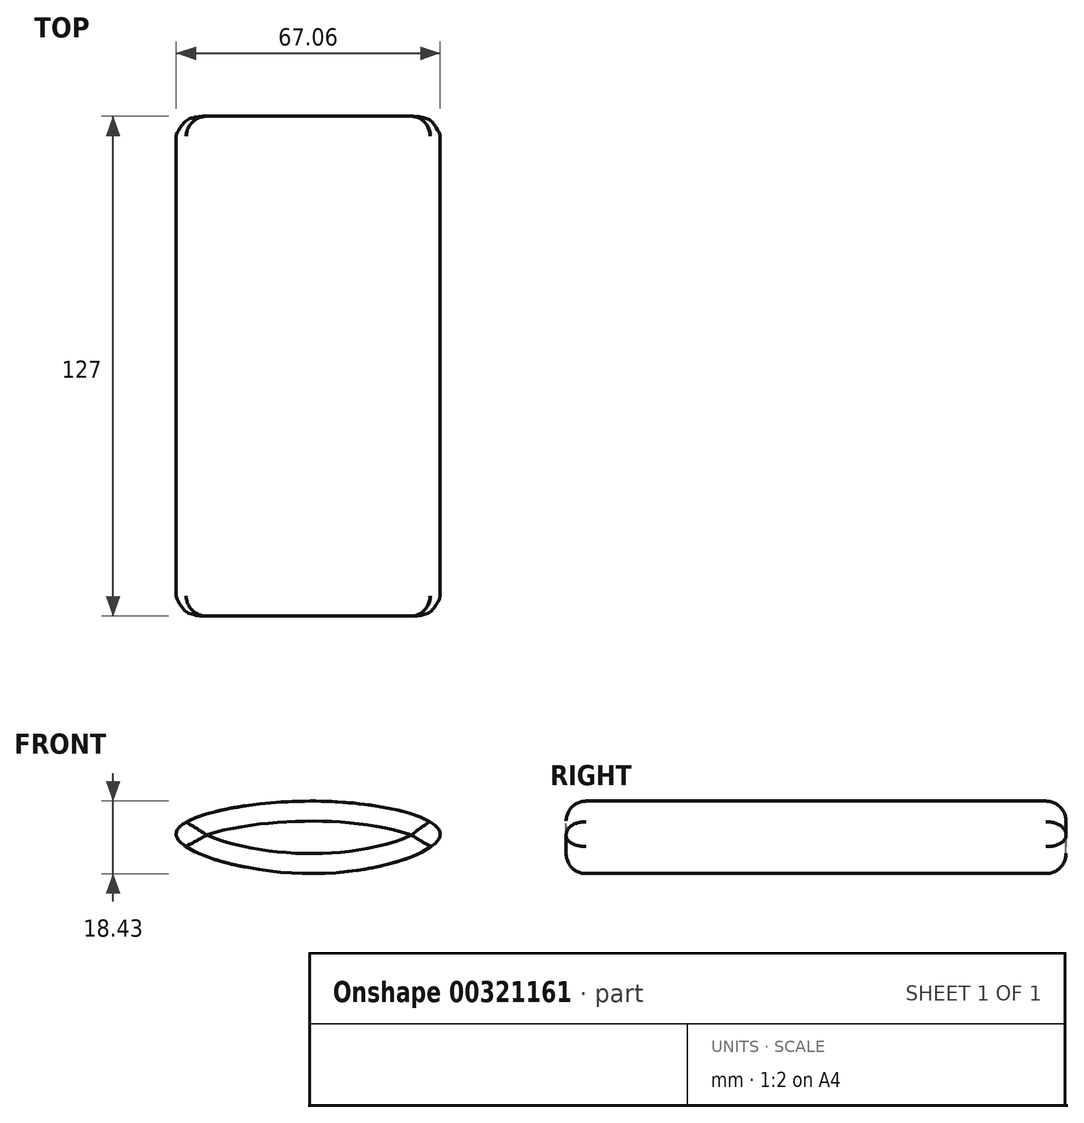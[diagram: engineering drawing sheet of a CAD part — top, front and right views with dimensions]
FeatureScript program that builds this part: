
annotation { "Feature Type Name" : "Feature", "Feature Type Description" : "" }
export const myFeature = defineFeature(function(context is Context, id is Id, definition is map)
    precondition{}
    {
        {
            var Q0;
            Q0=qCreatedBy(makeId("Front.planeOp"),FACE);
            var sketch = newSketch(context, id + "F0", { "sketchPlane" : qUnion([Q0])});
            skFitSpline(sketch, "E0", {"points": [v(-35.11, 0) * mm, v(0, 8.35) * mm, v(31.95, 0) * mm, v(0, -10.07) * mm, v(-35.11, 0) * mm]});
            skSolve(sketch);
        }
        {
            var Q0;
            Q0=makeQuery(id+"F0.imprint","IMPRINT",FACE,{"disambiguationData":[TD([[makeQuery(id+"F0.imprint","IMPRINT",EDGE,{"derivedFrom":sQuery(id+"F0.wireOp",EDGE,"E0")}),-1.0]])]});
            extrude(context, id + "F1", {"entities" : qUnion([Q0]), "depth" : 127 * mm});
        }
        {
            var Q0;
            Q0=makeQuery(id+"F1.opExtrude","CAP_EDGE",EDGE,{"disambiguationData":[OSD([sQuery(id+"F0.wireOp",EDGE,"E0")])],"isStart":false});
            var Q1;
            Q1=makeQuery(id+"F1.opExtrude","CAP_EDGE",EDGE,{"disambiguationData":[OSD([sQuery(id+"F0.wireOp",EDGE,"E0")])],"isStart":true});
            fillet(context, id + "F2", {"entities" : qUnion([Q0, Q1]), "radius" : 5.08 * mm, "tangentPropagation" : true, "allowEdgeOverflow" : false});
        }
    });
